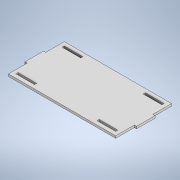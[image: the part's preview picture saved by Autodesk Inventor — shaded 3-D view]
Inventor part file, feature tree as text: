
AUTODESK INVENTOR PART (.ipt)
format: ipt  version: 2020 (Build 240168000, 168)  size: 170,496 bytes
history: native  units: in
note: dims shown in document units (in); Inventor stores cm internally (conversion verified against a paired STEP export)
features: extrude x5, sketch x5
ambient origin geometry x8: Origin, YZ Plane, XZ Plane, XY Plane, X Axis, Y Axis, Z Axis, Center Point
bodies: Solid1 (feature_tree)
feature tree (10):
  extrude  "Extrusion1"  Depth=1.1811in TaperAngle=0.0deg
  extrude  "Extrusion2"  Depth=0.3937in
  extrude  "Extrusion3"  Depth=0.3937in
  extrude  "Extrusion4"  Depth=1.1811in
  extrude  "Extrusion5"  Depth=0.1969in TaperAngle=0.0deg
  sketch  "Sketch1"  dims[d9=0.1181in d10=0.0in d30=1.1811in d31=0.0in]
  sketch  "Sketch2"  dims[d35=0.3937in d36=0.3937in]
  sketch  "Sketch3"  dims[d39=0.3937in d40=0.3937in]
  sketch  "Sketch4"  dims[d41=1.1811in d42=0.0in d43=0.5906in]
  sketch  "Sketch5"  dims[d44=0.5906in d45=0.3937in d46=0.0in d47=0.1181in d48=0.0in d49=0.1969in d50=0.0344in]
